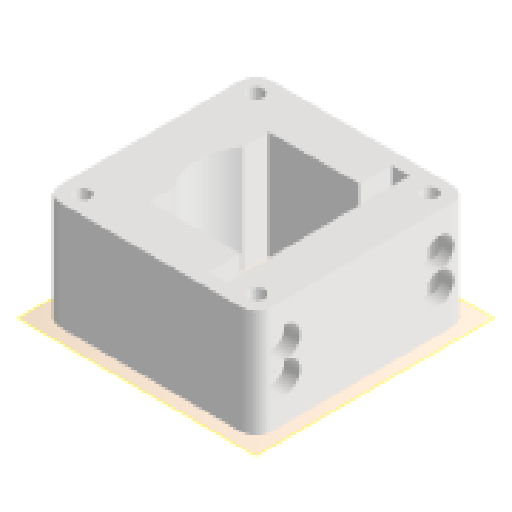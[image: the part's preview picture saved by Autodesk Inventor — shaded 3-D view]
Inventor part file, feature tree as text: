
AUTODESK INVENTOR PART (.ipt)
format: ipt  version: 2024.1 (Build 281209000, 209)  size: 220,672 bytes
history: native  units: mm
features: reference x6, sketch x3, other x3, plane x2, extrude x2, hole x1
ambient origin geometry x8: Origin, YZ Plane, XZ Plane, XY Plane, X Axis, Y Axis, Z Axis, Center Point
bodies: Volumenkörper1 (feature_tree)
feature tree (17):
  plane  "Arbeitsebene1"
  sketch  "Skizze1"  dims[d0=28.0mm d1=28.0mm]
  plane  "Arbeitsebene2"
  extrude  "Extrusion1"  Depth=28.0mm
  extrude  "Extrusion2"  Depth=10.0mm
  hole  "Bohrung1"  [1 undecoded]
  reference  "Referenz1"
  sketch  "Skizze2"  dims[d2=2.0mm d3=10.0mm]
  reference  "Referenz2"
  reference  "Referenz3"
  reference  "Referenz4"
  reference  "Referenz5"
  sketch  "Skizze3"  dims[d4=10.0mm d5=0.0mm d6=0.2mm d7=0.2mm d8=0.2mm d9=0.2mm d10=10.0mm d11=0.0mm d12=1.8mm d13=6.0mm d14=4.0mm d15=2.0mm d16=90.0deg d17=8.0mm d18=20.594885mm]
  reference  "Referenz6"
  other  "Assembly_Planktoscope_Uc2version_wormdrive_V3.iam"
  other  "60_Planktoscope_Base_half_wormdrive_1:1"
  other  "00_Micro_Stepper_15mm_Gearbox:1"
note: 1 required parameter value undecoded (feature->parameter linkage not recoverable at this tier; creation-order binding heuristic only, values carry confidence <= 0.55)
